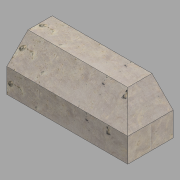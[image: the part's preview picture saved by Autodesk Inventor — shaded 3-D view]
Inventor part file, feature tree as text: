
AUTODESK INVENTOR PART (.ipt)
format: ipt  version: 2022.1 (Build 261234020, 234B)  size: 124,928 bytes
history: native  units: in
note: dims shown in document units (in); Inventor stores cm internally (conversion verified against a paired STEP export)
features: other x3, mirror x1
ambient origin geometry x8: Origin, YZ Plane, XZ Plane, XY Plane, X Axis, Y Axis, Z Axis, Center Point
bodies: Solid1 (feature_tree)
feature tree (4):
  other  "Return_L.ipt"
  mirror  "Mirror1"
  other  "Solid1::Return_L.ipt"
  other  "TaggingFeature1"
